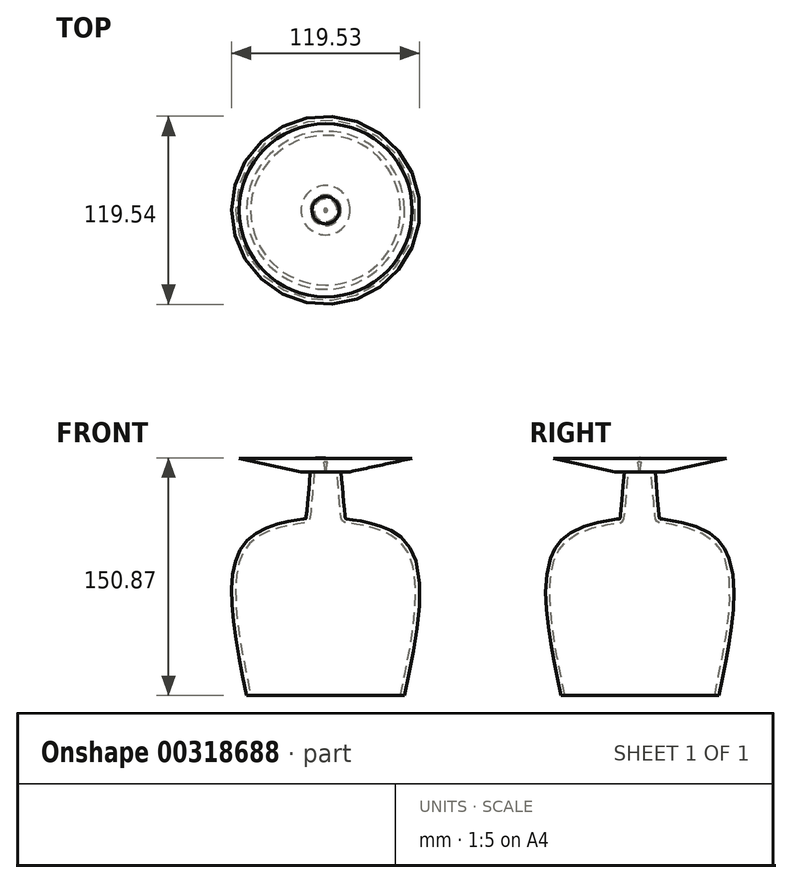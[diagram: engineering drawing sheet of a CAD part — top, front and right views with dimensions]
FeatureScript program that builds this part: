
annotation { "Feature Type Name" : "Feature", "Feature Type Description" : "" }
export const myFeature = defineFeature(function(context is Context, id is Id, definition is map)
    precondition{}
    {
        {
            var Q0;
            Q0=qCreatedBy(makeId("Front.planeOp"),FACE);
            var sketch = newSketch(context, id + "F0", { "sketchPlane" : qUnion([Q0])});
            skLineSegment(sketch, "E0", {"start": v(0, 75.98) * mm, "end": v(0, -75.44) * mm, "construction": true});
            skSolve(sketch);
        }
        {
            var Q0;
            Q0=qCreatedBy(makeId("Front.planeOp"),FACE);
            var sketch = newSketch(context, id + "F1", { "sketchPlane" : qUnion([Q0])});
            skLineSegment(sketch, "E1", {"start": v(-14.9, 75.97) * mm, "end": v(-14.9, 67.9) * mm});
            skLineSegment(sketch, "E2", {"start": v(-14.9, 67.9) * mm, "end": v(-9.78, 67.9) * mm});
            skFitSpline(sketch, "E3", {"points": [v(-9.78, 67.9) * mm, v(-12.46, 38.32) * mm, v(-13, 37.78) * mm, v(-48.89, 25.16) * mm, v(-50.18, -74.36) * mm], "startDerivative": vector(-13.96, -168.72) * mm, "endDerivative": vector(57.52, -278.33) * mm});
            skLineSegment(sketch, "E4", {"start": v(-50.18, -74.36) * mm, "end": v(0, -74.36) * mm});
            skLineSegment(sketch, "E5", {"start": v(0, -74.36) * mm, "end": v(0, 76.5) * mm});
            skLineSegment(sketch, "E6", {"start": v(0, 76.5) * mm, "end": v(-14.9, 75.97) * mm});
            skSolve(sketch);
        }
        {
            var Q0;
            Q0=makeQuery(id+"F1.imprint","IMPRINT",FACE,{"disambiguationData":[TD([[makeQuery(id+"F1.imprint","IMPRINT",EDGE,{"derivedFrom":sQuery(id+"F1.wireOp",EDGE,"E1")}),1.0]])]});
            var Q1;
            Q1=sQuery(id+"F1.wireOp",EDGE,"E5");
            revolve(context, id + "F2", {"entities" : qUnion([Q0]), "axis" : qUnion([Q1]), "revolveType" : RevolveType.FULL});
        }
        {
            var Q0;
            Q0=makeQuery(id+"F2.opRevolve","SWEPT_FACE",FACE,{"disambiguationData":[OSD([sQuery(id+"F1.wireOp",EDGE,"E4")])]});
            shell(context, id + "F3", {"entities" : qUnion([Q0]), "thickness" : 2.54 * mm});
        }
        {
            var Q0;
            Q0=qCreatedBy(makeId("Front.planeOp"),FACE);
            var sketch = newSketch(context, id + "F4", { "sketchPlane" : qUnion([Q0])});
            skLineSegment(sketch, "E7", {"start": v(15.62, 67.66) * mm, "end": v(54.98, 76.2) * mm});
            skLineSegment(sketch, "E8", {"start": v(0.22, 67.66) * mm, "end": v(15.62, 67.66) * mm});
            skLineSegment(sketch, "E9", {"start": v(54.98, 76.2) * mm, "end": v(1.5, 76.2) * mm});
            skLineSegment(sketch, "E10", {"start": v(1.5, 76.2) * mm, "end": v(0.22, 67.66) * mm});
            skSolve(sketch);
        }
        {
            var Q0;
            Q0=makeQuery(id+"F4.imprint","IMPRINT",FACE,{"disambiguationData":[TD([[makeQuery(id+"F4.imprint","IMPRINT",EDGE,{"derivedFrom":sQuery(id+"F4.wireOp",EDGE,"E7")}),1.0]])]});
            var Q1;
            Q1=sQuery(id+"F0.wireOp",EDGE,"E0");
            revolve(context, id + "F5", {"operationType" : NewBodyOperationType.ADD, "entities" : qUnion([Q0]), "axis" : qUnion([Q1]), "revolveType" : RevolveType.FULL});
        }
    });
